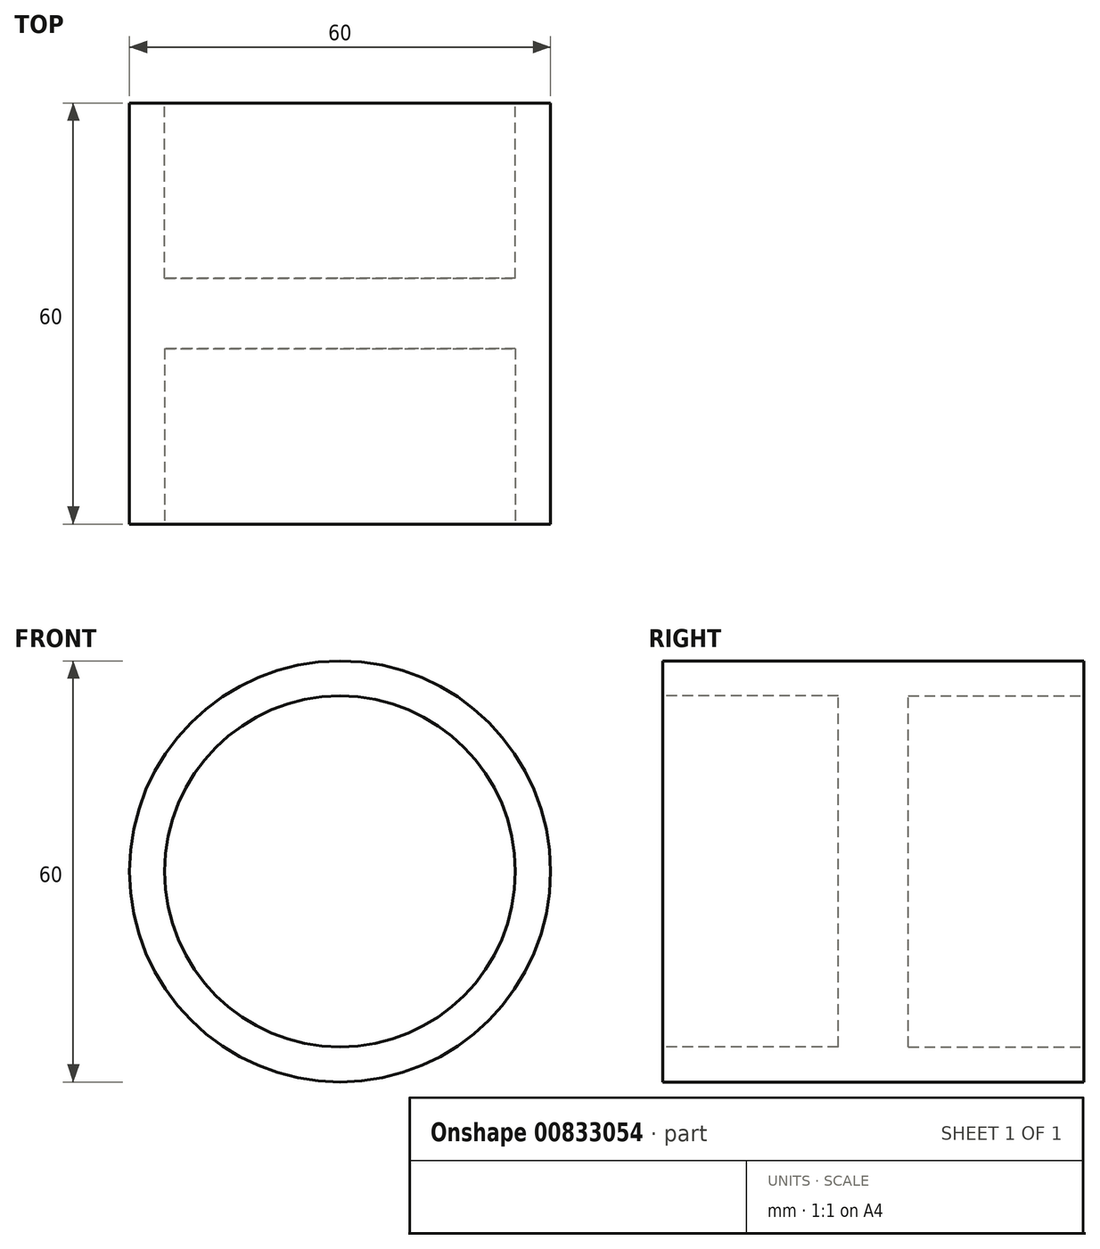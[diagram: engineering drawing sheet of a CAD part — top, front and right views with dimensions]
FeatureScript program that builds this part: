
annotation { "Feature Type Name" : "Feature", "Feature Type Description" : "" }
export const myFeature = defineFeature(function(context is Context, id is Id, definition is map)
    precondition{}
    {
        {
            var Q0;
            Q0=qCreatedBy(makeId("Front.planeOp"),FACE);
            var sketch = newSketch(context, id + "F0", { "sketchPlane" : qUnion([Q0])});
            skCircle(sketch, "E0", {"center": v(0, 0) * mm, "radius": 30 * mm});
            skSolve(sketch);
        }
        {
            var Q0;
            Q0=makeQuery(id+"F0.imprint","IMPRINT",FACE,{"disambiguationData":[TD([[makeQuery(id+"F0.imprint","IMPRINT",EDGE,{"derivedFrom":sQuery(id+"F0.wireOp",EDGE,"E0")}),1.0]])]});
            extrude(context, id + "F1", {"entities" : qUnion([Q0]), "depth" : 30 * mm, "offsetDistance" : 25 * mm});
        }
        {
            var Q0;
            Q0=makeQuery(id+"F1.opExtrude","CAP_FACE",FACE,{"disambiguationData":[OSD([sQuery(id+"F0.wireOp",EDGE,"E0")])],"isStart":false});
            var sketch = newSketch(context, id + "F2", { "sketchPlane" : qUnion([Q0])});
            skCircle(sketch, "E1", {"center": v(0, 0) * mm, "radius": 25 * mm});
            skSolve(sketch);
        }
        {
            var Q0;
            Q0=makeQuery(id+"F2.imprint","IMPRINT",FACE,{"disambiguationData":[TD([[makeQuery(id+"F2.imprint","IMPRINT",EDGE,{"derivedFrom":sQuery(id+"F2.wireOp",EDGE,"E1")}),1.0]])]});
            extrude(context, id + "F3", {"entities" : qUnion([Q0]), "operationType" : NewBodyOperationType.REMOVE, "oppositeDirection" : true, "depth" : 25 * mm, "offsetDistance" : 25 * mm});
        }
        {
            var Q0;
            Q0=makeQuery(id+"F1.opExtrude","SWEPT_BODY",BODY,{"disambiguationData":[OSD([sQuery(id+"F0.wireOp",EDGE,"E0")])]});
            var Q1;
            Q1=qCreatedBy(makeId("Front.planeOp"),FACE);
            mirror(context, id + "F4", {"operationType" : NewBodyOperationType.ADD, "entities" : qUnion([Q0]), "mirrorPlane" : qUnion([Q1])});
        }
    });
